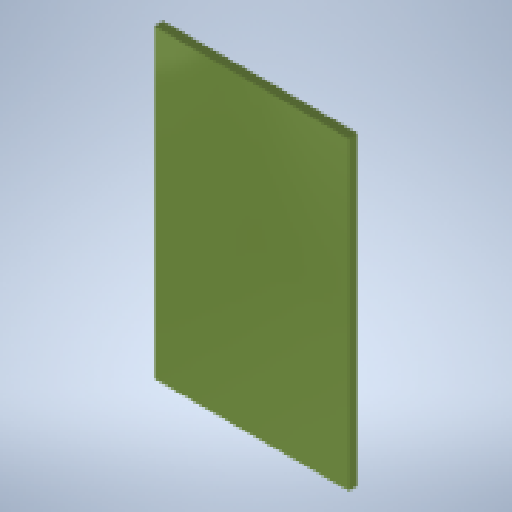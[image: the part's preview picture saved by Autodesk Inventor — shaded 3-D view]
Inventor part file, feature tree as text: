
AUTODESK INVENTOR PART (.ipt)
format: ipt  version: 2024.3 (Build 283343000, 343)  size: 208,384 bytes
history: native  units: mm
features: extrude x1, sketch x1
ambient origin geometry x8: Origin, YZ Plane, XZ Plane, XY Plane, X Axis, Y Axis, Z Axis, Center Point
bodies: Solid1 (feature_tree)
feature tree (2):
  extrude  "Extrusion1"  Depth=69.0mm
  sketch  "Sketch1"  dims[d0=44.0mm d1=69.0mm d2=44.0mm d3=69.0mm d4=2.0mm d5=0.0mm]
